# Revit family: NX_High_Mount_Outdoor_Sensor_Module
name_source: partatom
category: Communication Devices
revit_build: Autodesk Revit 2014 (Build: 20130308_1515(x64)
units: mm (PartAtom-declared; Revit-internal decimal feet)

## types (2) — shared parameters
Assembly Code = D5090
Certifications = Bluetooth Version 4.1,FCC Part 15.247,FCC ID: YH9NXSMP,
IC: 9044A-NXSMP
Default Elevation = 48 "
Description = The Hubbell Control Solutions NXSMP Low Mount Sensor
Module provides a unique solution for integrating automatic
control functions directly into a luminaire.
Features = • Compact, discrete, low profile luminaire sensor
• PIR motion sensor for automatic On/Off control
• Integrated daylight sensor for daylight
harvesting and/or lumen maintenance
• Bluetooth radio provides wireless control of luminaire
• Easy sensor configuration using smart device app
• Enables Intelliscope™ feature when paired with NX Bluetooth
mobile App, providing real time visibility of motion for improved
accuracy of sensor sensitivity and time delay adjustments
• Non-volatile memory for sensor settings
• Simple plug-in connection to NX Fixture Modules
Housing Material = Paint - Hubbell - Matte White
Manufacturer = Hubbell Control Solutions
Model = High Mount Indoor/Outdoor Sensor Module
Mounting = Mounts in 1.5” diameter aperture, secured by supplied nut on threaded body
Recommended max mounting height 45’ indoors, 30’ outdoors, min 16’
Power Requirements = 12VDC, 30 mA supplied by NXFM or NXRC
Product Documentation Link = https://hubbellcdn.com
Product Page URL = https://www.hubbell.com
Sensing Element = Metal-Hubbell-Nickel
Technology = Passive Infrared
Timer Timeout = Automatic mode:1 sec - 20 min
Type Comments = Outdoor Sensor
URL = https://www.hubbell.com
Warranty = 5-Years Warranty

## type names
- NXSMP-HMO
- NXSMP-HMO-A
type visibility flags (boolean, named after types; folded from table):
- NXSMP-HMO: Yes: (none)
- NXSMP-HMO-A: Yes: NXSMP-HMO-A

## geometry (parser evidence)
native form markers: Sweep x2
no freeform markers — native parametric forms only
